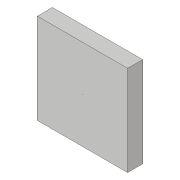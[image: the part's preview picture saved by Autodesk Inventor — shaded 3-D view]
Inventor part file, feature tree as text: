
AUTODESK INVENTOR PART (.ipt)
format: ipt  version: 2019 (Build 230136000, 136)  size: 80,896 bytes
history: native  units: in
note: dims shown in document units (in); Inventor stores cm internally (conversion verified against a paired STEP export)
features: extrude x2, sketch x2
ambient origin geometry x8: Origin, YZ Plane, XZ Plane, XY Plane, X Axis, Y Axis, Z Axis, Center Point
bodies: Solid1 (feature_tree)
feature tree (4):
  extrude  "Extrusion1"  Depth=4.7244in
  extrude  "Extrusion2"  Depth=0.7874in
  sketch  "Sketch1"  dims[d0=4.7244in d1=4.7244in]
  sketch  "Sketch2"  dims[d2=0.7874in d3=0.0in d4=2.3622in d5=0.0138in d6=0.0138in d7=0.7874in d8=0.0in]
